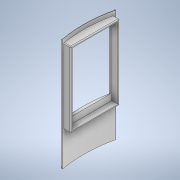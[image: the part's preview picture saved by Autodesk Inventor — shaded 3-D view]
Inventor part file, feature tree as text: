
AUTODESK INVENTOR PART (.ipt)
format: ipt  version: 2022 (Build 260153000, 153)  size: 235,008 bytes
history: native  units: mm
features: extrude x12, fillet x3, sketch x1
ambient origin geometry x8: Origin, YZ Plane, XZ Plane, XY Plane, X Axis, Y Axis, Z Axis, Center Point
bodies: Solid1 (feature_tree)
feature tree (16):
  sketch  "Sketch1"  dims[d14=75.0mm d15=4.5mm d16=68.0mm d17=2.0mm d18=2.0mm d19=2.0mm d20=2.0mm d21=2.0mm d22=32.0mm d23=26.0mm d24=26.0mm d26=28.0mm d27=28.0mm d29=2.0mm d30=7.5mm d31=7.5mm d32=2.0mm d33=138.0mm d34=0.0mm d35=133.0mm d36=0.0mm d37=131.0mm d38=0.0mm d39=129.0mm d40=0.0mm d41=131.0mm d42=0.0mm d43=129.0mm d44=0.0mm d45=51.0mm d46=0.0mm d47=51.0mm d48=0.0mm d49=43.0mm d50=0.0mm d51=41.0mm d52=0.0mm d53=43.0mm d54=0.0mm d55=41.0mm d56=0.0mm d57=1.0mm d58=1.5mm d59=1.5mm d60=0.0mm d61=0.0mm d62=0.0mm]
  extrude  "Extrusion1"  Depth=1.5mm
  extrude  "Extrusion2"  Depth=1.5mm
  extrude  "Extrusion3"  Depth=1.5mm
  extrude  "Extrusion4"  Depth=1.5mm
  extrude  "Extrusion5"  Depth=1.5mm
  extrude  "Extrusion6"  Depth=1.5mm
  extrude  "Extrusion7"  Depth=1.5mm
  extrude  "Extrusion8"  Depth=1.5mm
  extrude  "Extrusion9"  Depth=1.5mm
  extrude  "Extrusion10"  Depth=1.5mm
  extrude  "Extrusion11"  Depth=1.5mm
  extrude  "Extrusion12"  Depth=1.5mm
  fillet  "Fillet1"  Radius=2.0mm
  fillet  "Fillet2"  Radius=7.5mm
  fillet  "Fillet3"  Radius=7.5mm
